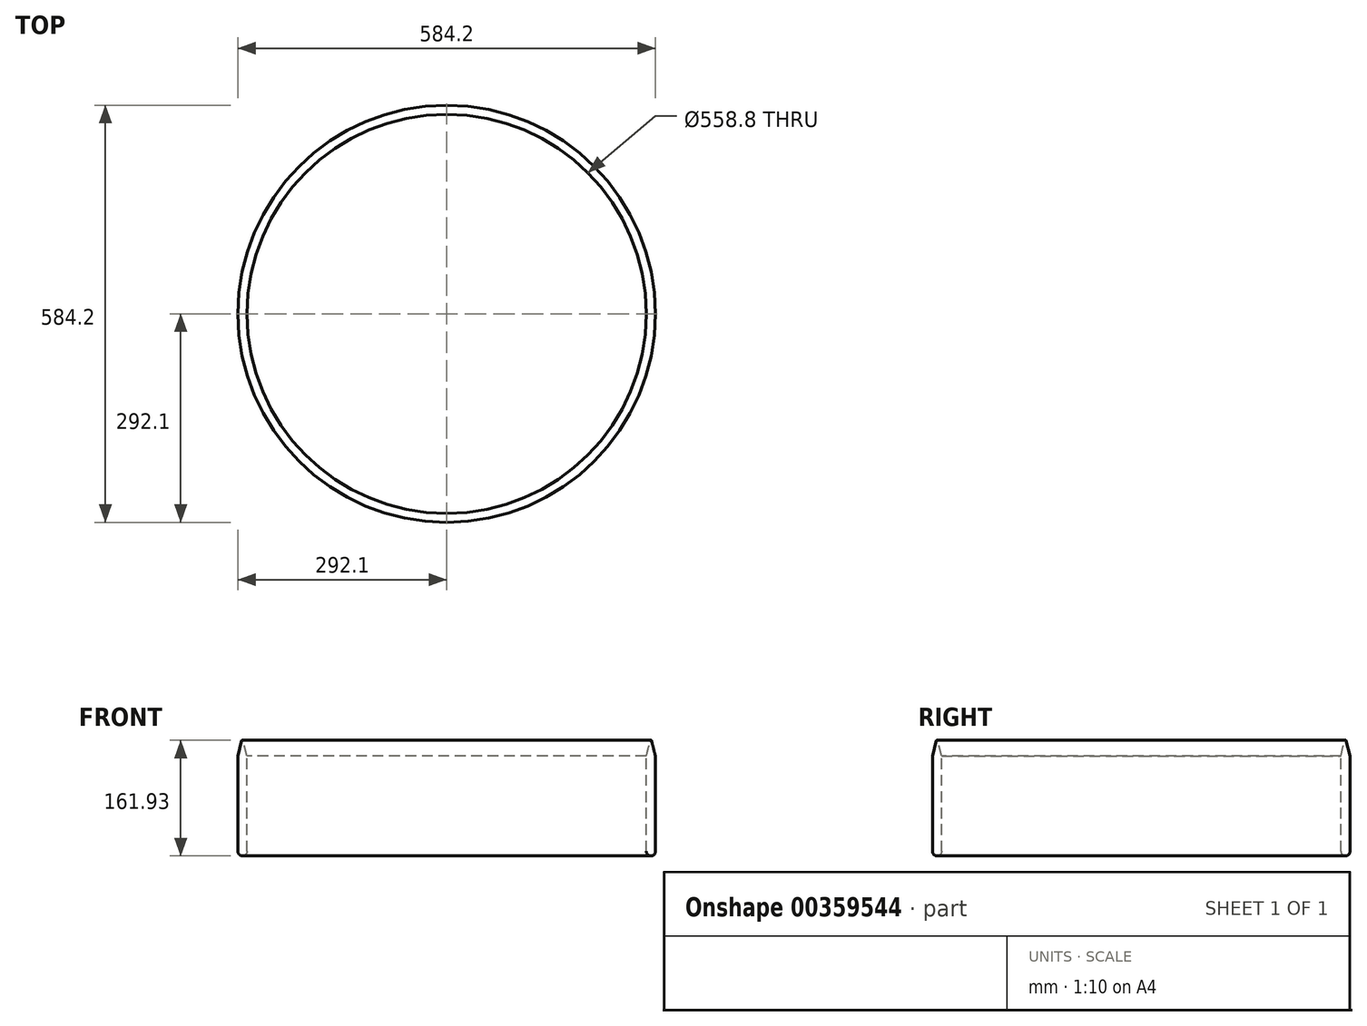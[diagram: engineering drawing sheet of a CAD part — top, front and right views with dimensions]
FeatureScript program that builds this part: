
annotation { "Feature Type Name" : "Feature", "Feature Type Description" : "" }
export const myFeature = defineFeature(function(context is Context, id is Id, definition is map)
    precondition{}
    {
        {
            var Q0;
            Q0=qCreatedBy(makeId("Front.planeOp"),FACE);
            var sketch = newSketch(context, id + "F0", { "sketchPlane" : qUnion([Q0])});
            skLineSegment(sketch, "E0.bottom", {"start": v(-279.4, -69.85) * mm, "end": v(-292.1, -69.85) * mm});
            skLineSegment(sketch, "E0.top", {"start": v(-279.4, 69.85) * mm, "end": v(-292.1, 69.85) * mm});
            skLineSegment(sketch, "E0.left", {"start": v(-279.4, -69.85) * mm, "end": v(-279.4, 69.85) * mm});
            skLineSegment(sketch, "E0.right", {"start": v(-292.1, -69.85) * mm, "end": v(-292.1, 69.85) * mm});
            skPoint(sketch, "E0.middle", {"position": v(-285.75, 0) * mm});
            skPoint(sketch, "E1", {"position": v(0, 0) * mm});
            skLineSegment(sketch, "E2", {"start": v(0, 4.02) * mm, "end": v(0, -4.92) * mm});
            skLineSegment(sketch, "E3", {"start": v(-292.1, 69.85) * mm, "end": v(-285.75, 95.25) * mm});
            skPoint(sketch, "E3.endSnap0", {"position": v(-285.75, 69.85) * mm});
            skLineSegment(sketch, "E4", {"start": v(-285.75, 95.25) * mm, "end": v(-279.4, 69.85) * mm});
            skLineSegment(sketch, "E5.MirrorCS", {"start": v(292.1, -69.85) * mm, "end": v(292.1, 69.85) * mm});
            skLineSegment(sketch, "E6.MirrorCS", {"start": v(279.4, -69.85) * mm, "end": v(279.4, 69.85) * mm});
            skLineSegment(sketch, "E7.MirrorCS", {"start": v(279.4, -69.85) * mm, "end": v(292.1, -69.85) * mm});
            skLineSegment(sketch, "E8.MirrorCS", {"start": v(292.1, 69.85) * mm, "end": v(285.75, 95.25) * mm});
            skLineSegment(sketch, "E9.MirrorCS", {"start": v(285.75, 95.25) * mm, "end": v(279.4, 69.85) * mm});
            skPoint(sketch, "E10.MirrorP", {"position": v(285.75, 69.85) * mm});
            skLineSegment(sketch, "E11", {"start": v(279.4, 69.85) * mm, "end": v(292.1, 69.85) * mm});
            skSolve(sketch);
        }
        {
            var Q0;
            Q0=makeQuery(id+"F0.imprint","IMPRINT",FACE,{"disambiguationData":[TD([[makeQuery(id+"F0.imprint","IMPRINT",EDGE,{"derivedFrom":sQuery(id+"F0.wireOp",EDGE,"E0.bottom")}),-1.0]])]});
            var Q1;
            Q1=makeQuery(id+"F0.imprint","IMPRINT",FACE,{"disambiguationData":[TD([[makeQuery(id+"F0.imprint","IMPRINT",EDGE,{"derivedFrom":sQuery(id+"F0.wireOp",EDGE,"E0.top")}),-1.0]])]});
            var Q2;
            Q2=sQuery(id+"F0.wireOp",EDGE,"E2");
            revolve(context, id + "F1", {"entities" : qUnion([Q0, Q1]), "axis" : qUnion([Q2]), "revolveType" : RevolveType.FULL});
        }
        {
            var Q0;
            Q0=makeQuery(id+"F1.opRevolve","SWEPT_EDGE",EDGE,{"disambiguationData":[OSD([sQuery(id+"F0.wireOp",EDGE,"E0.bottom"),sQuery(id+"F0.wireOp",EDGE,"E0.right")])]});
            var Q1;
            Q1=makeQuery(id+"F1.opRevolve","SWEPT_EDGE",EDGE,{"disambiguationData":[OSD([sQuery(id+"F0.wireOp",EDGE,"E0.bottom"),sQuery(id+"F0.wireOp",EDGE,"E0.left")])]});
            fillet(context, id + "F2", {"entities" : qUnion([Q0, Q1]), "radius" : 6.35 * mm, "tangentPropagation" : true, "allowEdgeOverflow" : false});
        }
        {
            var Q0;
            Q0=makeQuery(id+"F1.opRevolve","SWEPT_EDGE",EDGE,{"disambiguationData":[OSD([sQuery(id+"F0.wireOp",EDGE,"E0.top"),sQuery(id+"F0.wireOp",EDGE,"E0.right"),sQuery(id+"F0.wireOp",EDGE,"E3")])]});
            var Q1;
            Q1=makeQuery(id+"F1.opRevolve","SWEPT_EDGE",EDGE,{"disambiguationData":[OSD([sQuery(id+"F0.wireOp",EDGE,"E3"),sQuery(id+"F0.wireOp",EDGE,"E4")])]});
            fillet(context, id + "F3", {"entities" : qUnion([Q0, Q1]), "radius" : 1.02 * mm, "tangentPropagation" : true, "allowEdgeOverflow" : false});
        }
    });
